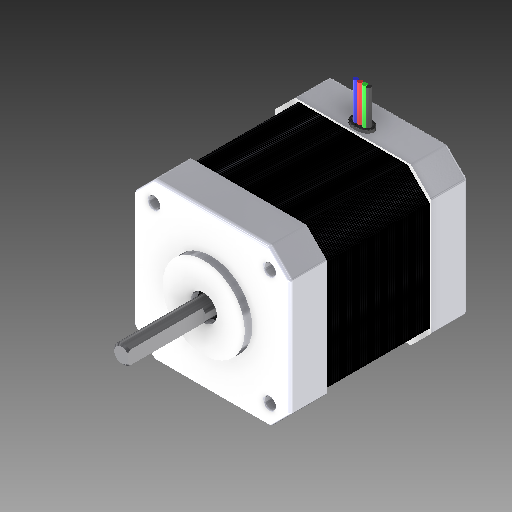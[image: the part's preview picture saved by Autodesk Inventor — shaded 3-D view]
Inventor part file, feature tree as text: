
AUTODESK INVENTOR PART (.ipt)
format: ipt  version: 2018 (Build 220112000, 112)  size: 1,184,256 bytes
history: native  units: mm
features: extrude x13, sketch x5, hole x4, fillet x4, chamfer x2, plane x1, pattern_linear x1, projected_geometry x1
ambient origin geometry x8: Origin, YZ Plane, XZ Plane, XY Plane, X Axis, Y Axis, Z Axis, Center Point
bodies: Solid1 (feature_tree)
feature tree (31):
  sketch  "Sketch1"  dims[d0=7.0mm d1=22.0mm]
  extrude  "Extrusion1"  Depth=22.0mm
  extrude  "Extrusion2"  Depth=31.0mm
  extrude  "Extrusion3"  Depth=3.0mm
  plane  "Work Plane2"
  extrude  "Extrusion7"  Depth=3.0mm
  extrude  "Extrusion8"  Depth=10.0mm
  chamfer  "Chamfer1"  Distance=42.0mm
  pattern_linear  "Rectangular Pattern2"  Spacing1=135.0deg  [1 undecoded]
  hole  "Hole1"  [1 undecoded]
  hole  "Hole2"  [1 undecoded]
  hole  "Hole3"  [1 undecoded]
  hole  "Hole4"  [1 undecoded]
  extrude  "Extrusion9"  Depth=10.0mm TaperAngle=0.0deg
  fillet  "Fillet1"  Radius=2.0mm
  fillet  "Fillet2"  Radius=48.0mm
  chamfer  "Chamfer2"  [1 undecoded]
  fillet  "Fillet3"  Radius=28.0mm
  sketch  "Sketch6"  dims[d10=3.0mm d11=3.0mm]
  extrude  "Extrusion10"  Depth=10.0mm
  fillet  "Fillet4"  Radius=1.0mm
  extrude  "Extrusion11"  Depth=10.0mm
  extrude  "Extrusion12"  Depth=10.0mm
  extrude  "Extrusion13"  Depth=10.0mm
  extrude  "Extrusion14"  Depth=10.0mm
  extrude  "Extrusion15"  Depth=10.0mm
  extrude  "Extrusion16"  Depth=10.0mm
  sketch  "Sketch4"  dims[d4=5.0mm d5=31.0mm]
  projected_geometry  "Projected Loop2"
  sketch  "Sketch5"  dims[d6=31.0mm d9=3.0mm]
  sketch  "Sketch11"  dims[d12=3.0mm d39=42.0mm d40=42.0mm d41=135.0deg d42=51.618795mm d43=51.618795mm d44=25.809398mm d45=25.809398mm d46=24.0mm d47=0.0mm d48=2.0mm d49=0.0mm d50=48.0mm d51=0.0mm d60=-10.0mm d126=28.0mm d127=0.0mm d128=1.0mm d129=1.0mm d130=1.0mm d131=1.0mm d132=0.5mm d134=0.5mm d135=0.5mm d136=0.5mm d137=0.5mm d138=1.0mm d139=1.0mm d140=0.5mm d141=0.0mm d145=0.125mm d146=2.0mm d147=45.0deg d148=560.0mm d150=0.5mm d151=10.0mm d152=10.0mm d153=6.0mm d154=6.0mm d155=4.0mm d156=2.0mm d157=90.0deg d158=3.0mm d159=0.0mm d160=10.0mm d161=10.0mm d162=6.0mm d163=6.0mm d164=4.0mm d165=2.0mm d166=90.0deg d167=3.0mm d168=0.0mm d169=10.0mm d170=10.0mm d171=6.0mm d172=6.0mm d173=4.0mm d174=2.0mm d175=90.0deg d176=3.0mm d177=0.0mm d178=10.0mm d179=10.0mm d180=6.0mm d181=6.0mm d182=4.0mm d183=2.0mm d184=90.0deg d185=3.0mm d186=0.0mm d187=48.0mm d188=0.0mm d189=47.0mm d190=0.0mm d191=1.0mm d192=1.0mm d193=0.5mm d194=2.0mm d195=45.0deg d196=0.5mm d197=1.2mm d198=40.0mm d200=1.2mm d201=10.0mm d203=10.0mm d205=2.5mm d206=2.5mm d207=1.0mm d208=0.0mm d209=0.3mm d210=10.0mm d211=0.0mm d212=10.0mm d213=0.0mm d214=10.0mm d215=0.0mm d216=10.0mm d217=0.0mm d218=0.2mm d219=5.0mm d220=0.0mm d221=0.0mm d225=20.0mm d226=0.0mm]
note: 6 required parameter values undecoded (feature->parameter linkage not recoverable at this tier; creation-order binding heuristic only, values carry confidence <= 0.55)
